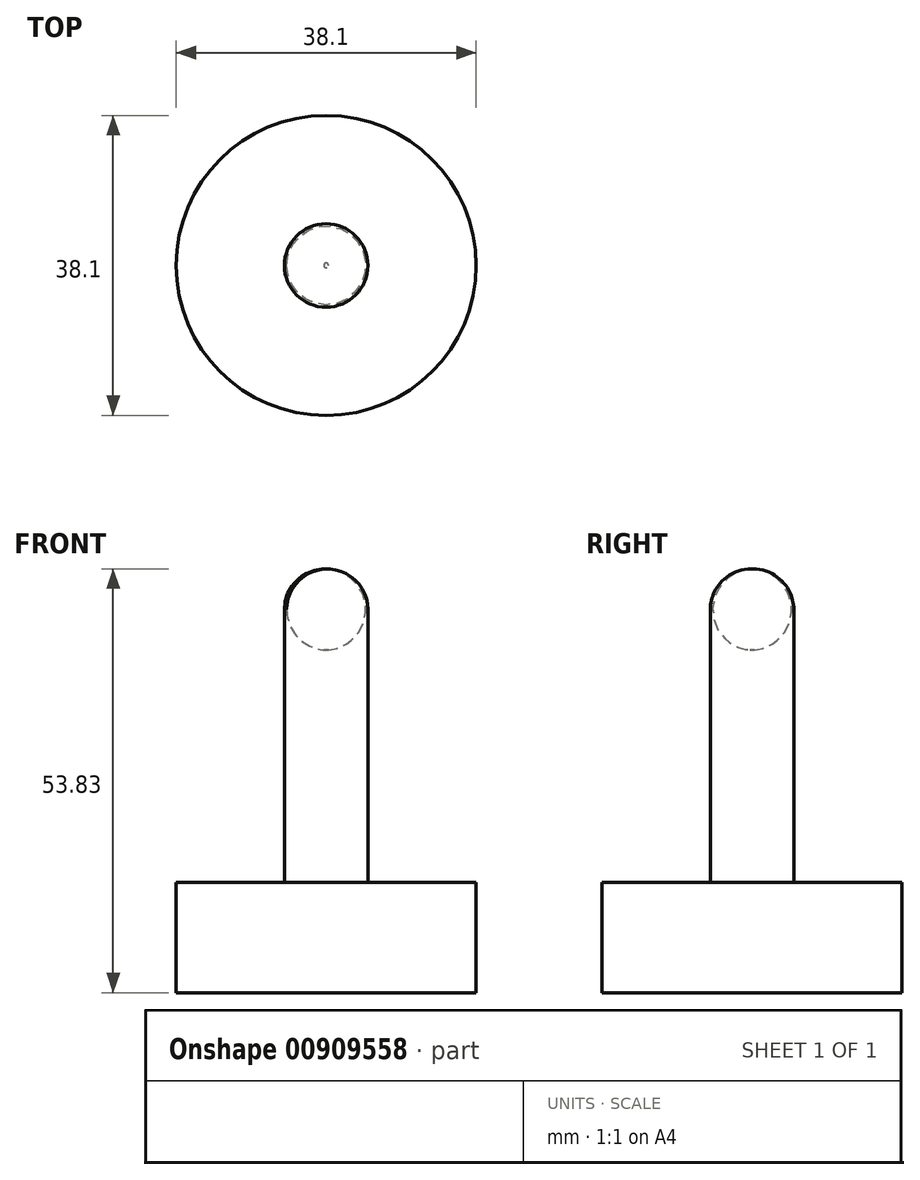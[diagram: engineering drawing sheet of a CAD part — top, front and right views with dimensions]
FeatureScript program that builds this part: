
annotation { "Feature Type Name" : "Feature", "Feature Type Description" : "" }
export const myFeature = defineFeature(function(context is Context, id is Id, definition is map)
    precondition{}
    {
        {
            var Q0;
            Q0=qCreatedBy(makeId("Front.planeOp"),FACE);
            var sketch = newSketch(context, id + "F0", { "sketchPlane" : qUnion([Q0])});
            skLineSegment(sketch, "E0", {"start": v(0, 0) * mm, "end": v(19.05, 0) * mm});
            skLineSegment(sketch, "E1", {"start": v(19.05, 0) * mm, "end": v(19.05, 14) * mm});
            skLineSegment(sketch, "E2", {"start": v(19.05, 14) * mm, "end": v(5.3, 14) * mm});
            skLineSegment(sketch, "E3", {"start": v(5.3, 14) * mm, "end": v(5.3, 48.68) * mm});
            skLineSegment(sketch, "E4", {"start": v(0, 0) * mm, "end": v(0, 53.83) * mm});
            skLineSegment(sketch, "E5", {"start": v(0, 53.83) * mm, "end": v(0, -8.57) * mm});
            skArc(sketch, "E6", {"start": v(5.3, 48.68) * mm, "mid": v(3.74, 52.37) * mm, "end": v(0, 53.83) * mm});
            skSolve(sketch);
        }
        {
            var Q0;
            {var subQ0=sQuery(id+"F0.wireOp",EDGE,"E0");Q0=makeQuery(id+"F0.imprint","IMPRINT",FACE,{"disambiguationData":[TD([[makeQuery(id+"F0.imprint","IMPRINT",EDGE,{"derivedFrom":subQ0}),1.0]])]});}
            var Q1;
            Q1=sQuery(id+"F0.wireOp",EDGE,"E5");
            revolve(context, id + "F1", {"surfaceOperationType" : NewSurfaceOperationType.NEW, "entities" : qUnion([Q0]), "axis" : qUnion([Q1]), "revolveType" : RevolveType.FULL});
        }
    });
